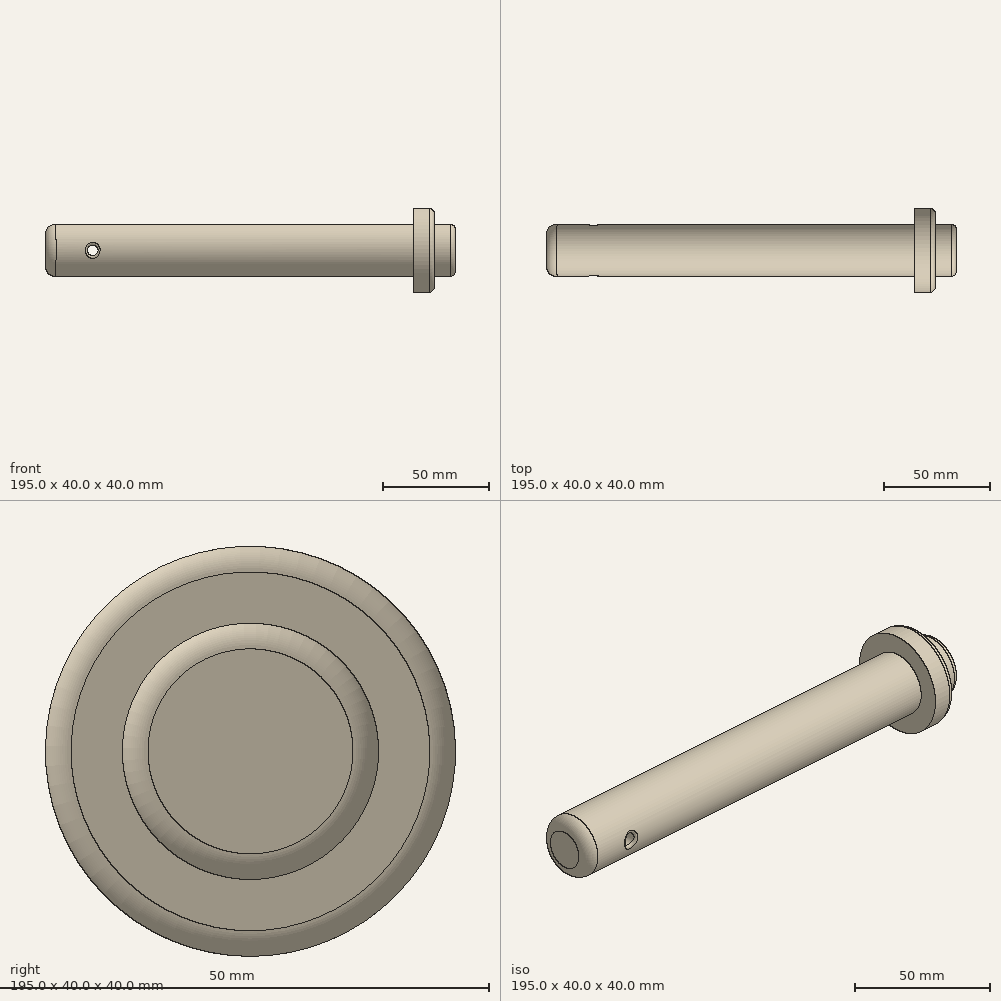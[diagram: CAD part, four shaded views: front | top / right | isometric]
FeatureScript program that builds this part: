
annotation { "Feature Type Name" : "Feature", "Feature Type Description" : "" }
export const myFeature = defineFeature(function(context is Context, id is Id, definition is map)
    precondition{}
    {
        {
            var Q0;
            Q0=qCreatedBy(makeId("Right.planeOp"),FACE);
            var sketch = newSketch(context, id + "F0", { "sketchPlane" : qUnion([Q0])});
            skCircle(sketch, "E0", {"center": v(0, 0) * mm, "radius": 12.5 * mm});
            skSolve(sketch);
        }
        {
            var Q0;
            Q0 = qSketchRegion(id + "F0", true);
            extrude(context, id + "F1", {"entities" : qUnion([Q0]), "depth" : 175 * mm});
        }
        {
            var Q0;
            Q0=makeQuery(id+"F1.opExtrude","CAP_FACE",FACE,{"disambiguationData":[OSD([sQuery(id+"F0.wireOp",EDGE,"E0")])],"isStart":false});
            var sketch = newSketch(context, id + "F2", { "sketchPlane" : qUnion([Q0])});
            skCircle(sketch, "E1", {"center": v(0, 0) * mm, "radius": 20 * mm});
            skSolve(sketch);
        }
        {
            var Q0;
            Q0 = qSketchRegion(id + "F2", true);
            extrude(context, id + "F3", {"entities" : qUnion([Q0]), "operationType" : NewBodyOperationType.ADD, "depth" : 10 * mm});
        }
        {
            var Q0;
            Q0=makeQuery(id+"F3.opExtrude","CAP_FACE",FACE,{"disambiguationData":[OSD([sQuery(id+"F2.wireOp",EDGE,"E1")])],"isStart":false});
            var sketch = newSketch(context, id + "F4", { "sketchPlane" : qUnion([Q0])});
            skCircle(sketch, "E2", {"center": v(0, 0) * mm, "radius": 12.5 * mm});
            skSolve(sketch);
        }
        {
            var Q0;
            Q0=makeQuery(id+"F4.imprint","IMPRINT",FACE,{"disambiguationData":[TD([[makeQuery(id+"F4.imprint","IMPRINT",EDGE,{"derivedFrom":sQuery(id+"F4.wireOp",EDGE,"E2")}),1.0]])]});
            extrude(context, id + "F5", {"entities" : qUnion([Q0]), "operationType" : NewBodyOperationType.ADD, "depth" : 10 * mm});
        }
        {
            var Q0;
            Q0=makeQuery(id+"F5.opExtrude","CAP_EDGE",EDGE,{"disambiguationData":[OSD([sQuery(id+"F4.wireOp",EDGE,"E2")])],"isStart":false});
            var Q1;
            Q1=makeQuery(id+"F3.opExtrude","CAP_EDGE",EDGE,{"disambiguationData":[OSD([sQuery(id+"F2.wireOp",EDGE,"E1")])],"isStart":false});
            fillet(context, id + "F6", {"entities" : qUnion([Q0, Q1]), "radius" : 2.5 * mm, "tangentPropagation" : true, "allowEdgeOverflow" : false});
        }
        {
            var Q0;
            Q0=qCreatedBy(makeId("Front.planeOp"),FACE);
            var sketch = newSketch(context, id + "F7", { "sketchPlane" : qUnion([Q0])});
            skCircle(sketch, "E3", {"center": v(22.5, 0) * mm, "radius": 2.5 * mm});
            skSolve(sketch);
        }
        {
            var Q0;
            Q0 = qSketchRegion(id + "F7", true);
            extrude(context, id + "F8", {"entities" : qUnion([Q0]), "operationType" : NewBodyOperationType.REMOVE, "endBound" : BoundingType.SYMMETRIC, "oppositeDirection" : true, "depth" : 25 * mm});
        }
        {
            var Q0;
            Q0=makeQuery(id+"F8.boolean.opBoolean","INTERSECT",EDGE,{"disambiguationData":[OD(0.0)],"derivedFrom":[makeQuery(id+"F1.opExtrude","SWEPT_FACE",FACE,{"disambiguationData":[OSD([sQuery(id+"F0.wireOp",EDGE,"E0")])]}),makeQuery(id+"F8.opExtrude","SWEPT_FACE",FACE,{"disambiguationData":[OSD([sQuery(id+"F7.wireOp",EDGE,"E3")])]})]});
            var Q1;
            Q1=makeQuery(id+"F8.boolean.opBoolean","INTERSECT",EDGE,{"disambiguationData":[OD(1.0)],"derivedFrom":[makeQuery(id+"F1.opExtrude","SWEPT_FACE",FACE,{"disambiguationData":[OSD([sQuery(id+"F0.wireOp",EDGE,"E0")])]}),makeQuery(id+"F8.opExtrude","SWEPT_FACE",FACE,{"disambiguationData":[OSD([sQuery(id+"F7.wireOp",EDGE,"E3")])]})]});
            fillet(context, id + "F9", {"entities" : qUnion([Q0, Q1]), "radius" : 1 * mm, "tangentPropagation" : true, "allowEdgeOverflow" : false});
        }
        {
            var Q0;
            Q0=makeQuery(id+"F1.opExtrude","CAP_EDGE",EDGE,{"disambiguationData":[OSD([sQuery(id+"F0.wireOp",EDGE,"E0")])],"isStart":true});
            fillet(context, id + "F10", {"entities" : qUnion([Q0]), "radius" : 5 * mm, "tangentPropagation" : true, "allowEdgeOverflow" : false});
        }
    });
